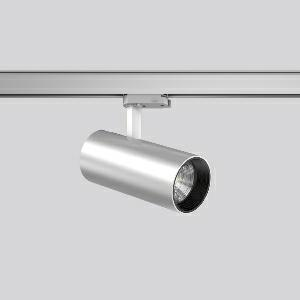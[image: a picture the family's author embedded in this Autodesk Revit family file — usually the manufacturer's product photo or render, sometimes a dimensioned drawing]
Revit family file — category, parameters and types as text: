
# Revit family: deecos_s_mini_742208_004_a754
name_source: partatom
category: Lighting Fixtures
units: mm (PartAtom-declared; Revit-internal decimal feet)

## family parameters
Cut with Voids When Loaded = No
Host = Face
Light Source = No
Part Type = Normal
Room Calculation Point = No
Round Connector Dimension = Use Diameter
Shared = No

## types (1)
- DEECOS S mini (1 x LED Modul 930, 2850 lm, 3000)
    Apparent Load = 29 VA
    Approval mark = CE
    CIE Flux Codes = 98 100 100 100 100
    Color Rendering = 90
    Color Temperature = 3000
    Default Elevation = 1800 mm
    Description = Series: DEECOS S mini
LED surface-mounted projector in modern design with no visible cooling ribs. Housing: die-cast aluminium, powder-coated. Rotation range: 356°. Swivel range: 90°. Black plastic ring and recessed LED to prevent glare from the side. Optical assembly with lens made of plastic (polycarbonate) for the best homogeneous light distribution - can be changed without tools. Best colour rendering index Ra>90. With multi adaptor for 3-circuit tracks 230 V. Suitable for Track on ceiling, Wall track. High quality converter without flickering and stroboscopic effect. The following accessories can be mounted without use of tools: interchangeable lenses, decorative glasses, honeycomb louvre, clear and frosted diffusers, white interchangeable plastic ring. 
Colour: silver
Diameter: 87 mm
Height: 214 mm
Lamp: LED
Socket: without socket
Colour temperature: 3000K
Colour rendering index (CRI): 92
System power: 29 W
Rated luminous flux: 2850 lm
Luminous efficiency: 98 lm/W
Control gear: Regulated power supply
Protection class: I
Type of protection: IP 20
    Height = 214 mm
    Lamp = 1 x LED Modul 930
    Lamp Light Flux = 2850 lm
    Lamp count = 1
    Length = 87 mm
    Lifetime = 50000 h
    Luminous efficacy = 98 lm/W
    Manufacturer = RZB
    ModVariant = No
    Model = 742208.004
    Mounting Place = Ceiling
    Mounting Type = Rail mounted
    Number of Poles = 1
    OnlyDefault = Yes
    Power Factor = 1
    Product Name = DEECOS S mini
    Product group = Track mounted projectors
    ProductGroupID = 301
    Protection Class = Protection class I
    Protection Degree = IP 20
    RLX_Detail_Level = 1
    RLX_Emergency_Light_Flux = 0 lm
    RLX_Emergency_Type = 0
    RLX_Emergency_Type_DB = No
    RlxData = <blob elided: 37413 chars, md5=4a2d2d41>
    Socket = socket
    Standby Power = 0 W
    System Light Flux = 2850 lm
    System Power = 29 W
    Type Comments = Product without accessories
    Type Image = 741930.004.jpg
    URL = http://relux.com
    VarID = ---
    Voltage = 230 V
    Voltage Range = 220-240 V
    Weight = 0.00 kg
    Width = 0 mm  [stored 0 ft]

note: [stored X ft] marks values corroborated as IEEE doubles in the binary element streams (Revit-internal decimal feet)

## geometry (parser evidence)
native form markers: Blend x4, Sweep x12
no freeform markers — native parametric forms only
